# Revit family: Boiler filling and draining valve with hose grommet 2512 01 (02)
name_source: partatom
category: Rohrzubehör
revit_build: Autodesk Revit 2018 (Build: 20190510_1515(x64)
units: mm (PartAtom-declared; Revit-internal decimal feet)

## family parameters
Arbeitsebenenbasiert = Nein
Beim Laden mit Abzugskörper schneiden = Nein
Bemaßung runder Anschluss = Durchmesser verwenden
Gemeinsam genutzt = Nein
Immer vertikal = Ja
OmniClass-Nummer = 23.65.55.14
OmniClass-Titel = Valves for Liquid Services
Teiletyp = Normal

## types (1)
- Boiler filling and draining valve with hose grommet 2512 01 (02)
    Application = the drain valves are installed as valves to fill and drain systems.
fields of application are building services, such as in heating or chilled water plant in buildings.
aromatic chlorinated hydrocarbons such as natural gas or petroleum occurring in, destroy the EPDM seals.
    Ball = forged brass CW617N, full bore, surface chrome plated
    Body = forged brass CW617N
    D03 = 15 mm  [stored 0.0492126 ft]
    D04 = 14 mm  [stored 0.0459318 ft]
    D05 = 11.9 mm  [stored 0.039042 ft]
    D06 = 7.5 mm  [stored 0.0246063 ft]
    D07 = 6.5 mm
    Handle = aluminium red painted
    Hersteller = Herz-Armaturen GmbH
    L04 = 4 mm  [stored 0.0131234 ft]
    L06 = 6.5 mm
    L07 = 3.5 mm  [stored 0.0114829 ft]
    L08 = 2 mm  [stored 0.00656168 ft]
    L09 = 13.4 mm  [stored 0.0439633 ft]
    L10 = 1 mm  [stored 0.00328084 ft]
    L100 = 14.6 mm  [stored 0.0479003 ft]
    L11 = 8.6 mm
    L12 = 3.8 mm
    LO1 = 2.5 mm  [stored 0.0082021 ft]
    Medium = heating water according ÖNORM H5195 or VDI-Standard 2035.
the use of ethylene, or propylene glycol in a mixing ratio 25-50% is allowed.
    R99 = 2 mm  [stored 0.00656168 ft]
    S04 = 6.5 mm
    SCRNCODE = 05;08;01
    SCRNSEQ = ARM;ARM_TYP="ABSV";1
    SCTWCODE = 01;10;01
    SCTWSEQ = ENT;AO;1
    Sealings = ball: PTFE; spindle: PTFE
    Spindle = brass CW614N
    URL = www.herzvalves.com
    W1 = 60.00°
    max. Operating pressure = 1000000.0 Pa
    max. Operating temperature = 110 °C
    min. Operating temperature = -30 °C

note: [stored X ft] marks values corroborated as IEEE doubles in the binary element streams (Revit-internal decimal feet)
